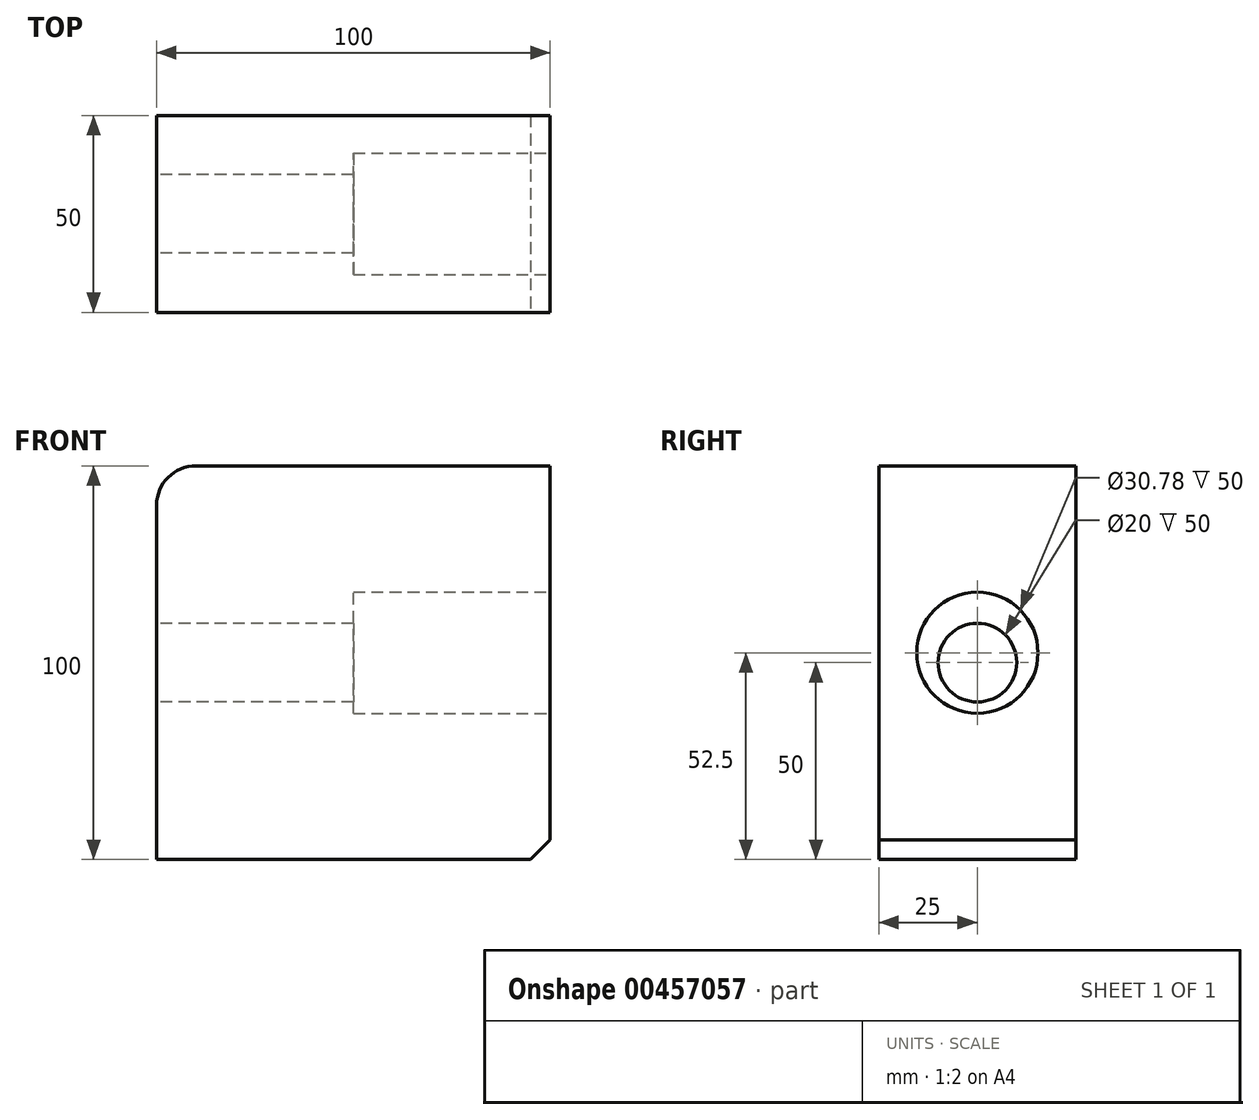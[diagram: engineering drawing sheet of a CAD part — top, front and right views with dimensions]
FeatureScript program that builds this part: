
annotation { "Feature Type Name" : "Feature", "Feature Type Description" : "" }
export const myFeature = defineFeature(function(context is Context, id is Id, definition is map)
    precondition{}
    {
        {
            var Q0;
            Q0=qCreatedBy(makeId("Front.planeOp"),FACE);
            var sketch = newSketch(context, id + "F0", { "sketchPlane" : qUnion([Q0])});
            skLineSegment(sketch, "E0.bottom", {"start": v(50, 50) * mm, "end": v(-50, 50) * mm});
            skLineSegment(sketch, "E0.top", {"start": v(50, -50) * mm, "end": v(-50, -50) * mm});
            skLineSegment(sketch, "E0.left", {"start": v(50, 50) * mm, "end": v(50, -50) * mm});
            skLineSegment(sketch, "E0.right", {"start": v(-50, 50) * mm, "end": v(-50, -50) * mm});
            skPoint(sketch, "E0.middle", {"position": v(0, 0) * mm});
            skSolve(sketch);
        }
        {
            var Q0;
            Q0 = qSketchRegion(id + "F0", true);
            extrude(context, id + "F1", {"entities" : qUnion([Q0]), "depth" : 50 * mm});
        }
        {
            var Q0;
            Q0=makeQuery(id+"F1.opExtrude","SWEPT_EDGE",EDGE,{"disambiguationData":[OSD([sQuery(id+"F0.wireOp",EDGE,"E0.bottom"),sQuery(id+"F0.wireOp",EDGE,"E0.right")])]});
            fillet(context, id + "F2", {"entities" : qUnion([Q0]), "radius" : 10 * mm, "tangentPropagation" : true, "allowEdgeOverflow" : false});
        }
        {
            var Q0;
            Q0=makeQuery(id+"F1.opExtrude","SWEPT_EDGE",EDGE,{"disambiguationData":[OSD([sQuery(id+"F0.wireOp",EDGE,"E0.top"),sQuery(id+"F0.wireOp",EDGE,"E0.left")])]});
            chamfer(context, id + "F3", {"entities" : qUnion([Q0]), "width" : 5 * mm, "tangentPropagation" : true});
        }
        {
            var Q0;
            Q0=makeQuery(id+"F1.opExtrude","SWEPT_FACE",FACE,{"disambiguationData":[OSD([sQuery(id+"F0.wireOp",EDGE,"E0.left")])]});
            var sketch = newSketch(context, id + "F4", { "sketchPlane" : qUnion([Q0])});
            skCircle(sketch, "E1", {"center": v(-25, 2.5) * mm, "radius": 15.4 * mm});
            skPoint(sketch, "E1.centerSnap0", {"position": v(-25, -45) * mm});
            skPoint(sketch, "E1.centerSnap1", {"position": v(-50, 2.5) * mm});
            skSolve(sketch);
        }
        {
            var Q0;
            Q0 = qSketchRegion(id + "F4", true);
            extrude(context, id + "F5", {"entities" : qUnion([Q0]), "operationType" : NewBodyOperationType.REMOVE, "oppositeDirection" : true, "depth" : 50 * mm});
        }
        {
            var Q0;
            Q0=makeQuery(id+"F1.opExtrude","SWEPT_FACE",FACE,{"disambiguationData":[OSD([sQuery(id+"F0.wireOp",EDGE,"E0.right")])]});
            var sketch = newSketch(context, id + "F6", { "sketchPlane" : qUnion([Q0])});
            skCircle(sketch, "E2", {"center": v(25, 0) * mm, "radius": 10 * mm});
            skPoint(sketch, "E2.centerSnap0", {"position": v(25, -50) * mm});
            skSolve(sketch);
        }
        {
            var Q0;
            Q0 = qSketchRegion(id + "F6", true);
            extrude(context, id + "F7", {"entities" : qUnion([Q0]), "operationType" : NewBodyOperationType.REMOVE, "oppositeDirection" : true, "depth" : 50 * mm});
        }
    });
